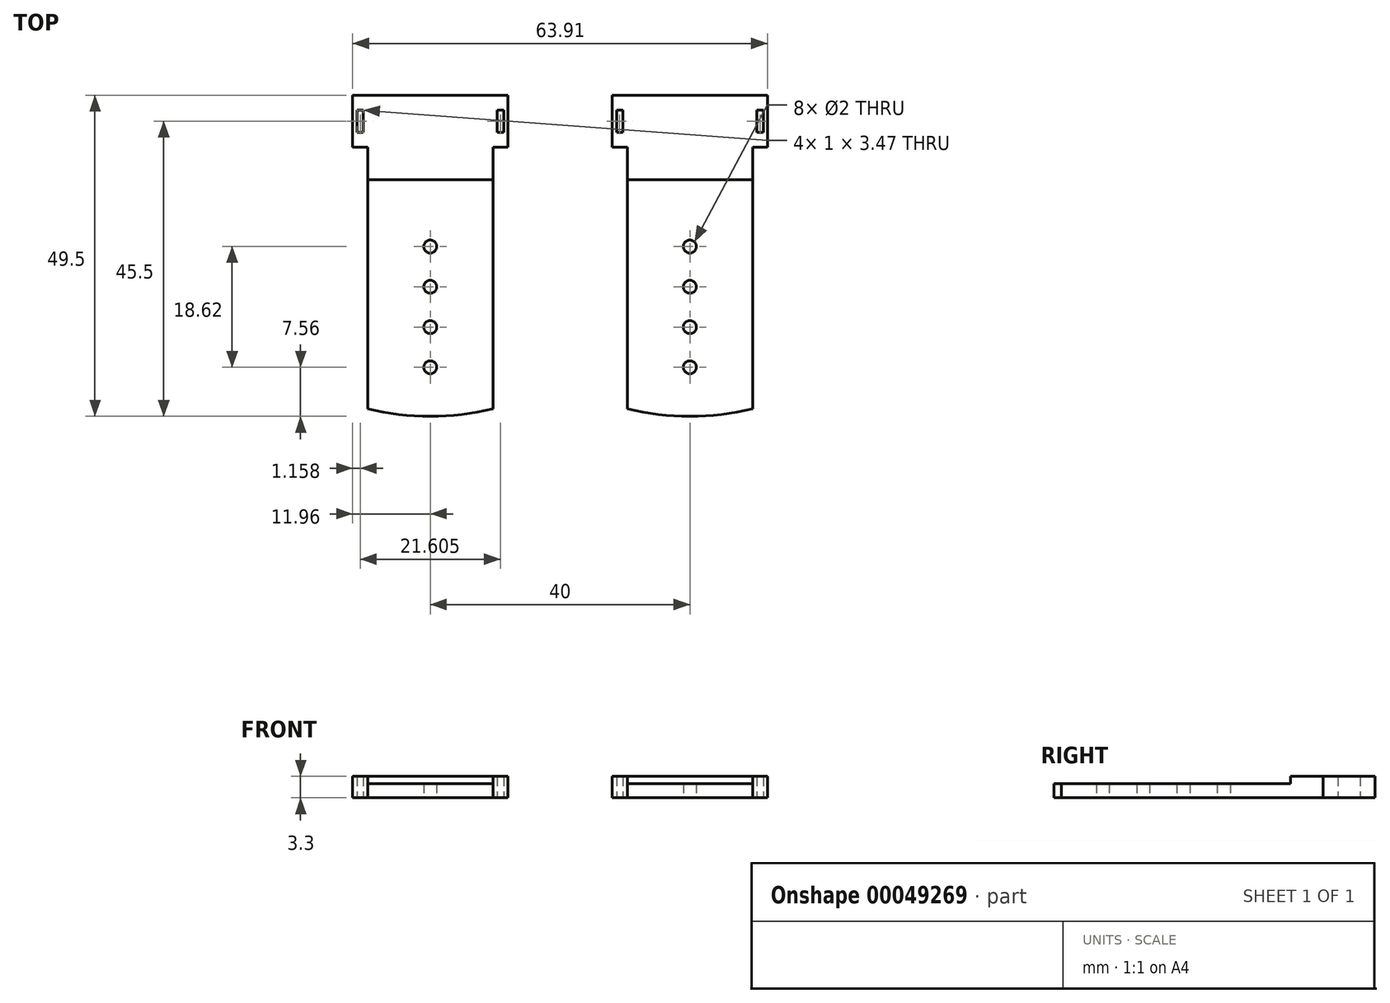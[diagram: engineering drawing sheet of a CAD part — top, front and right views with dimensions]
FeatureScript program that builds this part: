
annotation { "Feature Type Name" : "Feature", "Feature Type Description" : "" }
export const myFeature = defineFeature(function(context is Context, id is Id, definition is map)
    precondition{}
    {
        {
            var Q0;
            Q0=qCreatedBy(makeId("Top.planeOp"),FACE);
            var sketch = newSketch(context, id + "F0", { "sketchPlane" : qUnion([Q0])});
            skLineSegment(sketch, "E0.bottom", {"start": v(-9.65, -18.25) * mm, "end": v(9.65, -18.25) * mm});
            skLineSegment(sketch, "E0.top", {"start": v(-9.65, 18.25) * mm, "end": v(9.65, 18.25) * mm});
            skLineSegment(sketch, "E0.left", {"start": v(-9.65, -18.25) * mm, "end": v(-9.65, 18.25) * mm});
            skLineSegment(sketch, "E0.right", {"start": v(9.65, -18.25) * mm, "end": v(9.65, 18.25) * mm});
            skLineSegment(sketch, "E1", {"start": v(0, 99.55) * mm, "end": v(0, -86.53) * mm, "construction": true});
            skLineSegment(sketch, "E2", {"start": v(-9.65, -18.25) * mm, "end": v(9.65, 18.25) * mm, "construction": true});
            skLineSegment(sketch, "E3", {"start": v(60.48, -17.09) * mm, "end": v(-55.9, -17.09) * mm, "construction": true});
            skArc(sketch, "E4", {"start": v(-9.65, -17.09) * mm, "mid": v(0, -18.25) * mm, "end": v(9.65, -17.09) * mm});
            skLineSegment(sketch, "E5.top", {"start": v(-9.65, 31.25) * mm, "end": v(9.65, 31.25) * mm});
            skLineSegment(sketch, "E5.left", {"start": v(-9.65, 18.25) * mm, "end": v(-9.65, 31.25) * mm});
            skLineSegment(sketch, "E5.right", {"start": v(9.65, 18.25) * mm, "end": v(9.65, 31.25) * mm});
            skLineSegment(sketch, "E6", {"start": v(-9.65, 23.25) * mm, "end": v(9.65, 23.25) * mm});
            skLineSegment(sketch, "E7", {"start": v(-8.62, 31.25) * mm, "end": v(-8.62, 23.25) * mm});
            skLineSegment(sketch, "E8.MirrorCS", {"start": v(8.62, 31.25) * mm, "end": v(8.62, 23.25) * mm});
            skLineSegment(sketch, "E9.bottom", {"start": v(-9.65, 23.25) * mm, "end": v(-11.95, 23.25) * mm});
            skLineSegment(sketch, "E9.top", {"start": v(-9.65, 31.25) * mm, "end": v(-11.95, 31.25) * mm});
            skLineSegment(sketch, "E9.left", {"start": v(-9.65, 23.25) * mm, "end": v(-9.65, 31.25) * mm});
            skLineSegment(sketch, "E9.right", {"start": v(-11.95, 23.25) * mm, "end": v(-11.95, 31.25) * mm});
            skLineSegment(sketch, "E10.MirrorCS", {"start": v(9.65, 31.25) * mm, "end": v(11.96, 31.25) * mm});
            skLineSegment(sketch, "E11.MirrorCS", {"start": v(11.95, 23.25) * mm, "end": v(11.95, 31.25) * mm});
            skLineSegment(sketch, "E12.MirrorCS", {"start": v(9.65, 23.25) * mm, "end": v(11.96, 23.25) * mm});
            skLineSegment(sketch, "E13", {"start": v(-11.95, 31.25) * mm, "end": v(-9.65, 23.25) * mm, "construction": true});
            skLineSegment(sketch, "E14.bottom", {"start": v(-10.3, 25.51) * mm, "end": v(-11.3, 25.51) * mm});
            skLineSegment(sketch, "E14.top", {"start": v(-10.3, 28.99) * mm, "end": v(-11.3, 28.99) * mm});
            skLineSegment(sketch, "E14.left", {"start": v(-10.3, 25.51) * mm, "end": v(-10.3, 28.99) * mm});
            skLineSegment(sketch, "E14.right", {"start": v(-11.3, 25.51) * mm, "end": v(-11.3, 28.99) * mm});
            skPoint(sketch, "E14.middle", {"position": v(-10.8, 27.25) * mm});
            skLineSegment(sketch, "E15.MirrorCS", {"start": v(11.3, 25.51) * mm, "end": v(11.3, 28.99) * mm});
            skLineSegment(sketch, "E16.MirrorCS", {"start": v(10.3, 25.51) * mm, "end": v(11.3, 25.51) * mm});
            skLineSegment(sketch, "E17.MirrorCS", {"start": v(10.3, 25.51) * mm, "end": v(10.3, 28.99) * mm});
            skLineSegment(sketch, "E18.MirrorCS", {"start": v(10.3, 28.99) * mm, "end": v(11.3, 28.99) * mm});
            skCircle(sketch, "E19", {"center": v(0, -10.7) * mm, "radius": 1 * mm});
            skCircle(sketch, "E20.0.1.0", {"center": v(0, -4.48) * mm, "radius": 1 * mm});
            skCircle(sketch, "E20.0.2.0", {"center": v(0, 1.72) * mm, "radius": 1 * mm});
            skCircle(sketch, "E20.0.3.0", {"center": v(0, 7.93) * mm, "radius": 1 * mm});
            skLineSegment(sketch, "E20.direction1", {"start": v(0, -10.7) * mm, "end": v(25, -10.7) * mm, "construction": true});
            skLineSegment(sketch, "E20.direction2", {"start": v(0, -10.7) * mm, "end": v(0, -4.48) * mm, "construction": true});
            skSolve(sketch);
        }
        {
            var Q0;
            {var subQ1=sQuery(id+"F0.wireOp",EDGE,"E0.top");Q0=makeQuery(id+"F0.imprint","IMPRINT",FACE,{"disambiguationData":[TD([[makeQuery(id+"F0.imprint","IMPRINT",EDGE,{"derivedFrom":subQ1}),-1.0]])]});}
            extrude(context, id + "F1", {"entities" : qUnion([Q0]), "depth" : 2.2 * mm});
        }
        {
            var Q0;
            {var subQ0=sQuery(id+"F0.wireOp",EDGE,"E7");Q0=makeQuery(id+"F0.imprint","IMPRINT",FACE,{"disambiguationData":[TD([[makeQuery(id+"F0.imprint","IMPRINT",EDGE,{"derivedFrom":subQ0}),1.0]])]});}
            var Q1;
            {var subQ4=sQuery(id+"F0.wireOp",EDGE,"E0.top");Q1=makeQuery(id+"F0.imprint","IMPRINT",FACE,{"disambiguationData":[TD([[makeQuery(id+"F0.imprint","IMPRINT",EDGE,{"derivedFrom":subQ4}),1.0]])]});}
            var Q2;
            {var subQ0=sQuery(id+"F0.wireOp",EDGE,"E7");Q2=makeQuery(id+"F0.imprint","IMPRINT",FACE,{"disambiguationData":[TD([[makeQuery(id+"F0.imprint","IMPRINT",EDGE,{"derivedFrom":subQ0}),-1.0]])]});}
            var Q3;
            {var subQ0=sQuery(id+"F0.wireOp",EDGE,"E9.bottom");Q3=makeQuery(id+"F0.imprint","IMPRINT",FACE,{"disambiguationData":[TD([[makeQuery(id+"F0.imprint","IMPRINT",EDGE,{"derivedFrom":subQ0}),-1.0]])]});}
            var Q4;
            {var subQ3=sQuery(id+"F0.wireOp",EDGE,"E8.MirrorCS");Q4=makeQuery(id+"F0.imprint","IMPRINT",FACE,{"disambiguationData":[TD([[makeQuery(id+"F0.imprint","IMPRINT",EDGE,{"derivedFrom":subQ3}),1.0]])]});}
            var Q5;
            {var subQ1=sQuery(id+"F0.wireOp",EDGE,"E10.MirrorCS");Q5=makeQuery(id+"F0.imprint","IMPRINT",FACE,{"disambiguationData":[TD([[makeQuery(id+"F0.imprint","IMPRINT",EDGE,{"derivedFrom":subQ1}),-1.0]])]});}
            extrude(context, id + "F2", {"entities" : qUnion([Q0, Q1, Q2, Q3, Q4, Q5]), "operationType" : NewBodyOperationType.ADD, "depth" : 3.3 * mm});
        }
        {
            var Q0;
            Q0=qCreatedBy(makeId("Right.planeOp"),FACE);
            cPlane(context, id + "F3", {"entities" : qUnion([Q0]), "cplaneType" : CPlaneType.OFFSET, "offset" : 20 * mm, "width" : 150 * mm, "height" : 150 * mm});
        }
        {
            var Q0;
            Q0=makeQuery(id+"F1.opExtrude","SWEPT_BODY",BODY,{"disambiguationData":[OSD([sQuery(id+"F0.wireOp",EDGE,"E0.top"),sQuery(id+"F0.wireOp",EDGE,"E0.left"),sQuery(id+"F0.wireOp",EDGE,"E0.right"),sQuery(id+"F0.wireOp",EDGE,"E4"),sQuery(id+"F0.wireOp",EDGE,"E19"),sQuery(id+"F0.wireOp",EDGE,"E20.0.1.0"),sQuery(id+"F0.wireOp",EDGE,"E20.0.2.0"),sQuery(id+"F0.wireOp",EDGE,"E20.0.3.0")])]});
            var Q1;
            Q1=qCreatedBy(id+"F3.planeOp",FACE);
            mirror(context, id + "F4", {"entities" : qUnion([Q0]), "mirrorPlane" : qUnion([Q1])});
        }
    });
